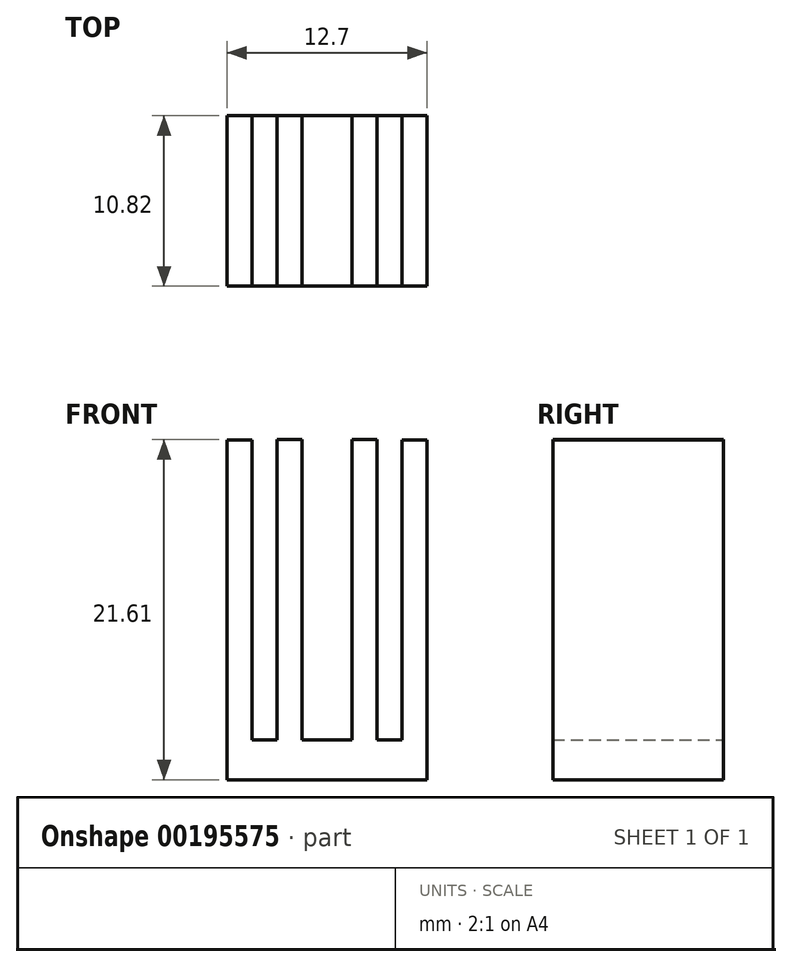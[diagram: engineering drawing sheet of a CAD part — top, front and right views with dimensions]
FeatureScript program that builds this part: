
annotation { "Feature Type Name" : "Feature", "Feature Type Description" : "" }
export const myFeature = defineFeature(function(context is Context, id is Id, definition is map)
    precondition{}
    {
        {
            var Q0;
            Q0=qCreatedBy(makeId("Front.planeOp"),FACE);
            var sketch = newSketch(context, id + "F0", { "sketchPlane" : qUnion([Q0])});
            skLineSegment(sketch, "E0.bottom", {"start": v(-6.35, 1.27) * mm, "end": v(6.35, 1.27) * mm});
            skLineSegment(sketch, "E0.top", {"start": v(-6.35, -1.27) * mm, "end": v(6.35, -1.27) * mm});
            skLineSegment(sketch, "E0.left", {"start": v(-6.35, 1.27) * mm, "end": v(-6.35, -1.27) * mm});
            skLineSegment(sketch, "E0.right", {"start": v(6.35, 1.27) * mm, "end": v(6.35, -1.27) * mm});
            skPoint(sketch, "E0.middle", {"position": v(0, 0) * mm});
            skLineSegment(sketch, "E1.bottom", {"start": v(-6.35, 1.27) * mm, "end": v(-4.76, 1.27) * mm});
            skLineSegment(sketch, "E1.top", {"start": v(-6.35, 20.32) * mm, "end": v(-4.76, 20.32) * mm});
            skLineSegment(sketch, "E1.left", {"start": v(-6.35, 1.27) * mm, "end": v(-6.35, 20.32) * mm});
            skLineSegment(sketch, "E1.right", {"start": v(-4.76, 1.27) * mm, "end": v(-4.76, 20.32) * mm});
            skLineSegment(sketch, "E2.bottom", {"start": v(6.35, 1.27) * mm, "end": v(4.76, 1.27) * mm});
            skLineSegment(sketch, "E2.top", {"start": v(6.35, 20.32) * mm, "end": v(4.76, 20.32) * mm});
            skLineSegment(sketch, "E2.left", {"start": v(6.35, 1.27) * mm, "end": v(6.35, 20.32) * mm});
            skLineSegment(sketch, "E2.right", {"start": v(4.76, 1.27) * mm, "end": v(4.76, 20.32) * mm});
            skSolve(sketch);
        }
        {
            var Q0;
            Q0=qSketchRegion(id+"F0",true);
            extrude(context, id + "F1", {"entities" : qUnion([Q0]), "depth" : 30.48 * mm});
        }
        {
            var Q0;
            Q0=makeQuery(id+"F1.opExtrude","CAP_FACE",FACE,{"disambiguationData":[OSD([sQuery(id+"F0.wireOp",EDGE,"E0.bottom"),sQuery(id+"F0.wireOp",EDGE,"E0.top"),sQuery(id+"F0.wireOp",EDGE,"E0.left"),sQuery(id+"F0.wireOp",EDGE,"E0.right"),sQuery(id+"F0.wireOp",EDGE,"E1.top"),sQuery(id+"F0.wireOp",EDGE,"E1.left"),sQuery(id+"F0.wireOp",EDGE,"E1.right"),sQuery(id+"F0.wireOp",EDGE,"E2.top"),sQuery(id+"F0.wireOp",EDGE,"E2.left"),sQuery(id+"F0.wireOp",EDGE,"E2.right")])],"isStart":false});
            extrude(context, id + "F2", {"entities" : qUnion([Q0]), "operationType" : NewBodyOperationType.REMOVE, "oppositeDirection" : true, "depth" : 19.66 * mm});
        }
        {
            var Q0;
            Q0=qCreatedBy(makeId("Front.planeOp"),FACE);
            var sketch = newSketch(context, id + "F3", { "sketchPlane" : qUnion([Q0])});
            skLineSegment(sketch, "E3.bottom", {"start": v(-3.18, 20.34) * mm, "end": v(-1.59, 20.34) * mm});
            skLineSegment(sketch, "E3.left", {"start": v(-3.18, 20.34) * mm, "end": v(-3.17, 1.29) * mm});
            skLineSegment(sketch, "E3.right", {"start": v(-1.59, 20.34) * mm, "end": v(-1.59, 1.29) * mm});
            skLineSegment(sketch, "E4.bottom", {"start": v(1.59, 20.34) * mm, "end": v(3.18, 20.34) * mm});
            skLineSegment(sketch, "E4.left", {"start": v(1.59, 20.34) * mm, "end": v(1.59, 1.29) * mm});
            skLineSegment(sketch, "E4.right", {"start": v(3.18, 20.34) * mm, "end": v(3.18, 1.29) * mm});
            skLineSegment(sketch, "E5", {"start": v(0, 20.37) * mm, "end": v(0, 0) * mm});
            skLineSegment(sketch, "E6", {"start": v(1.59, 1.29) * mm, "end": v(1.59, 0) * mm});
            skLineSegment(sketch, "E7", {"start": v(3.18, 1.29) * mm, "end": v(3.18, 0) * mm});
            skLineSegment(sketch, "E8", {"start": v(3.18, 0) * mm, "end": v(1.59, 0) * mm});
            skLineSegment(sketch, "E9", {"start": v(-3.17, 1.29) * mm, "end": v(-3.17, 0) * mm});
            skLineSegment(sketch, "E10", {"start": v(-1.59, 1.29) * mm, "end": v(-1.59, 0) * mm});
            skLineSegment(sketch, "E11", {"start": v(-1.59, 0) * mm, "end": v(-3.17, 0) * mm});
            skSolve(sketch);
        }
        {
            var Q0;
            Q0=makeQuery(id+"F3.imprint","IMPRINT",FACE,{"disambiguationData":[TD([[makeQuery(id+"F3.imprint","IMPRINT",EDGE,{"derivedFrom":sQuery(id+"F3.wireOp",EDGE,"E3.bottom")}),-1.0]])]});
            var Q1;
            Q1=makeQuery(id+"F3.imprint","IMPRINT",FACE,{"disambiguationData":[TD([[makeQuery(id+"F3.imprint","IMPRINT",EDGE,{"derivedFrom":sQuery(id+"F3.wireOp",EDGE,"E4.bottom")}),-1.0]])]});
            extrude(context, id + "F4", {"entities" : qUnion([Q0, Q1]), "operationType" : NewBodyOperationType.ADD, "depth" : 10.82 * mm});
        }
    });
